# Revit family: QF_COO_Vintos PLUS 13xGN11
name_source: partatom
category: Sonderausstattung
revit_build: Autodesk Revit 2018 (Build: 20170223_1515(x64)
units: mm (PartAtom-declared; Revit-internal decimal feet)

## family parameters
Arbeitsebenenbasiert = Nein
Beim Laden mit Abzugskörper schneiden = Nein
Bemaßung runder Anschluss = Durchmesser verwenden
Gemeinsam genutzt = Nein
Immer vertikal = Ja
Raumberechnungspunkt = Nein
Teiletyp = Normal

## types (2) — shared parameters
Anlaufstrom = 35 A
Beschreibung = Schnellkühler / Schockfroster
Betriebsstrom = 8 A
Elektrische leistung = 4100 W
Fließstrom = 5 A
Hersteller = Cool Compact Kühlgeräte GmbH
Höhe = 2008 mm  [stored 6.58793 ft]
Internetadresse Gerätehersteller = www.coolcompact.de
Internetadresse für Ersatzteilliste = www.coolcompact.de
Internetadresse für die Maßzeichnung = www.coolcompact.de
Internetadresse für kritische Ersatzteilliste = www.coolcompact.de
Kondensat Leitung = 19 mm
Kälte Betriebsdruck = 1800000.0 Pa
Kälte Externer Kompressor = Nein
Kälte Tauwasserablauf = Ja
Kälte Verdampfungstemperatur = -10 °C
Kälteleistung = 7630 W
Kältemittel = R452a
Kältemittelmenge = 3000
Länge Gerätebreite = 790 mm  [stored 2.59186 ft]
Maximale Geräteabsicherung = 16 A
Minimale Stromaufnahme = 12 A
Modell = 13 x GN1/1 Vintos +
Phasen = 3
Siphon am Gerät = Nein
Spannung = 400 V
Stecker System = CEE 16A
Tiefe = 970 mm  [stored 3.18241 ft]
URL = www.coolcompact.de
Zubehör = Ja
Zuleitung zum Gerät im Lieferumfang = Ja

## per-type parameters (varying)
| type | Beschreibung durch Hersteller analog Leistungsverzeichnislangtext | Gerätegewicht Netto | Kälte Abmessung Flüssigkeitsleitung | Kälte Abmessung Saugleitung |
| Vintos PLUS 13 x GN1/1_SKFMEQ1311D-VP | Schnellkühler / Schockfroster, Multifunktionsgerät, steckerfertig | 288.00 kg | 0 mm  [stored 0 ft] | 0 mm  [stored 0 ft] |
| Vintos PLUS 13 x GN1/1_SKFZKQ1311D-VP | Schnellkühler / Schockfroster, Multifunktionsgerät, zum Anschluß an separate Einzelmaschine | 200.00 kg | 12 mm  [stored 0.0393701 ft] | 18 mm  [stored 0.0590551 ft] |

note: [stored X ft] marks values corroborated as IEEE doubles in the binary element streams (Revit-internal decimal feet)
